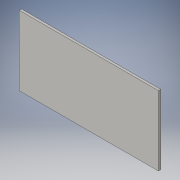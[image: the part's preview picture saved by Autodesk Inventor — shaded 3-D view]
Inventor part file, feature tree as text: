
AUTODESK INVENTOR PART (.ipt)
format: ipt  version: 2016 (Build 200138000, 138)  size: 89,600 bytes
history: native  units: in
note: dims shown in document units (in); Inventor stores cm internally (conversion verified against a paired STEP export)
features: sketch x2, extrude x1, direct_edit x1, hole x1, move_body x1
ambient origin geometry x8: Origin, YZ Plane, XZ Plane, XY Plane, X Axis, Y Axis, Z Axis, Center Point
bodies: Solid1 (feature_tree)
feature tree (6):
  extrude  "Extrusion1"  Depth=3.0in
  sketch  "Sketch2"  dims[d2=0.1in d3=0.0in d4=0.0in d5=0.0in d6=-3.0in d7=0.25in d8=0.75in d9=0.375in d10=0.25in d11=0.5635in d12=1.0in d13=0.8108in]
  direct_edit  "Direct Edit1"
  hole  "Hole1"  [1 undecoded]
  sketch  "Sketch1"  dims[d0=9.0in d1=3.0in]
  move_body  "Move1"
note: 1 required parameter value undecoded (feature->parameter linkage not recoverable at this tier; creation-order binding heuristic only, values carry confidence <= 0.55)
